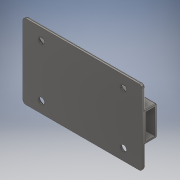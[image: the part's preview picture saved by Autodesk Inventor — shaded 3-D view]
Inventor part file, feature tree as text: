
AUTODESK INVENTOR PART (.ipt)
format: ipt  version: 2018 (Build 220112000, 112)  size: 219,648 bytes
history: native  units: mm
features: fillet x5, sketch x4, extrude x3, hole x1
ambient origin geometry x8: Origin, YZ Plane, XZ Plane, XY Plane, X Axis, Y Axis, Z Axis, Center Point
bodies: Solid1 (feature_tree)
feature tree (13):
  extrude  "Extrusion1"  Depth=50.0mm
  sketch  "Sketch2"  dims[d2=2.5mm d3=0.0mm d4=4.0mm]
  extrude  "Extrusion3"  Depth=4.0mm
  extrude  "Extrusion4"  Depth=4.0mm
  fillet  "Fillet2"  Radius=4.0mm
  fillet  "Fillet3"  Radius=55.0mm
  hole  "Hole1"  [1 undecoded]
  fillet  "Fillet4"  Radius=12.5mm
  fillet  "Fillet5"  Radius=20.0mm
  fillet  "Fillet6"  Radius=7.5mm
  sketch  "Sketch1"  dims[d0=80.0mm d1=50.0mm]
  sketch  "Sketch3"  dims[d5=4.0mm d6=4.0mm d7=4.0mm d8=55.0mm]
  sketch  "Sketch4"  dims[d9=35.0mm d10=7.5mm d11=12.5mm d14=20.0mm d15=7.5mm d16=7.5mm d17=17.0mm d18=1.5mm d19=77.5mm d20=0.0mm d21=35.0mm d22=10.0mm d23=20.0mm d24=1.5mm d25=0.0mm d27=1.0mm d28=2.0mm d29=4.0mm d30=5.984mm d31=8.0mm d32=2.0mm d33=90.0deg d34=8.0mm d35=20.594885mm d36=1.0mm d37=1.5mm d38=0.5mm]
note: 1 required parameter value undecoded (feature->parameter linkage not recoverable at this tier; creation-order binding heuristic only, values carry confidence <= 0.55)
